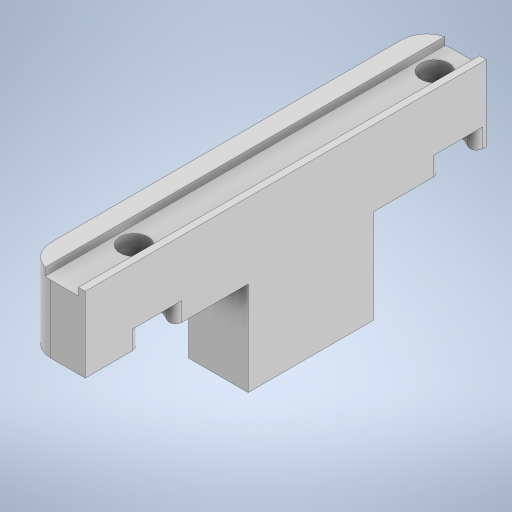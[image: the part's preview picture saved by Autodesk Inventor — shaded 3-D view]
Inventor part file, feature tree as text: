
AUTODESK INVENTOR PART (.ipt)
format: ipt  version: 2024 (Build 280153000, 153)  size: 312,832 bytes
history: native  units: in
note: dims shown in document units (in); Inventor stores cm internally (conversion verified against a paired STEP export)
features: extrude x4, sketch x4, projected_geometry x4, fillet x2
ambient origin geometry x8: Origin, YZ Plane, XZ Plane, XY Plane, X Axis, Y Axis, Z Axis, Center Point
bodies: Solid1 (feature_tree)
feature tree (14):
  extrude  "Extrusion1"  Depth=2.5197in
  extrude  "Extrusion2"  Depth=1.8898in
  extrude  "Extrusion3"  Depth=0.4724in TaperAngle=0.0deg
  fillet  "Fillet1"  Radius=0.0433in
  fillet  "Fillet2"  Radius=0.2126in
  extrude  "Extrusion5"  Depth=0.4724in TaperAngle=0.0deg
  sketch  "Sketch1"  dims[d1=0.374in d2=2.5197in]
  sketch  "Sketch2"  dims[d3=0.1772in d4=1.8898in]
  sketch  "Sketch3"  dims[d6=0.1457in d7=0.4724in d8=0.0in d9=0.0433in d10=0.2126in]
  sketch  "Sketch4"  dims[d11=0.0472in d12=0.4724in d13=0.0in d14=0.2953in d15=0.1181in d16=0.0in d17=0.1772in d18=0.0394in d19=0.1575in d20=0.7874in d21=0.5315in d24=0.5906in d25=0.0in d76=0.4724in d42=0.0197in d43=0.0344in d44=0.0197in d45=0.0344in d46=0.0in d47=0.0in d48=0.0in d49=0.0in d50=0.0in d51=0.0in d52=0.0in d53=0.0in d55=0.0197in d56=0.0344in d57=0.0197in d58=0.0344in d60=0.0197in d61=0.0344in d62=0.0197in d63=0.0344in d72=0.0197in d73=0.0344in d74=0.0197in d75=0.0344in]
  projected_geometry  "Projected Loop2"
  projected_geometry  "Projected Loop3"
  projected_geometry  "Projected Loop4"
  projected_geometry  "Projected Loop5"
